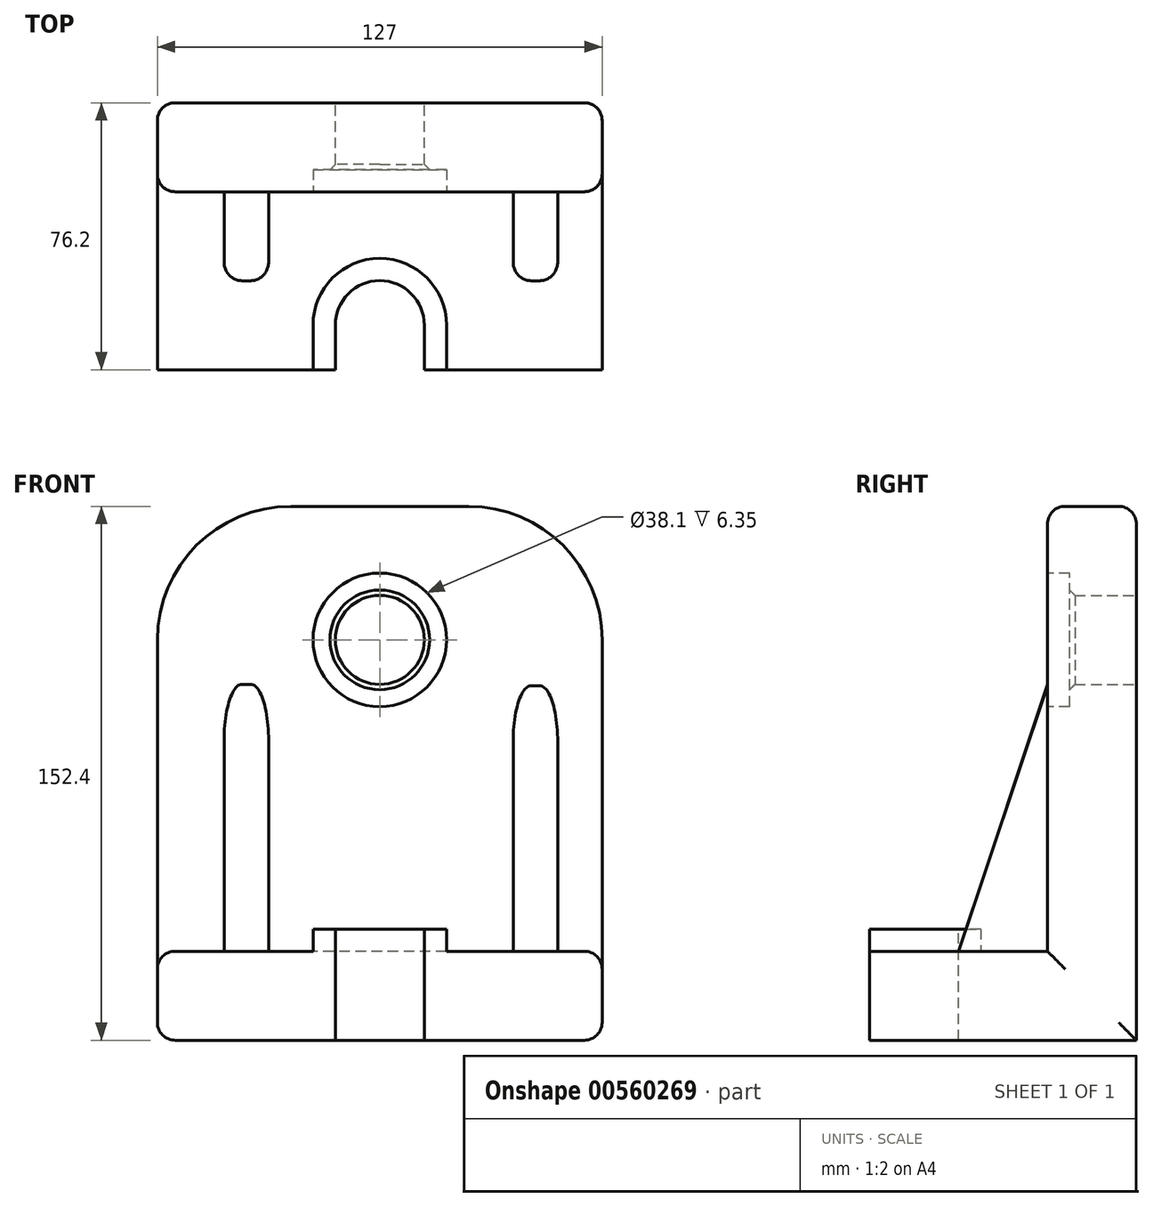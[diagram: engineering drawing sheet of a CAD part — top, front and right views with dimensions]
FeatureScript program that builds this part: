
annotation { "Feature Type Name" : "Feature", "Feature Type Description" : "" }
export const myFeature = defineFeature(function(context is Context, id is Id, definition is map)
    precondition{}
    {
        {
            var Q0;
            Q0=qCreatedBy(makeId("Right.planeOp"),FACE);
            var sketch = newSketch(context, id + "F0", { "sketchPlane" : qUnion([Q0])});
            skLineSegment(sketch, "E0", {"start": v(0, 25.4) * mm, "end": v(0, 152.4) * mm});
            skLineSegment(sketch, "E1", {"start": v(0, 152.4) * mm, "end": v(-25.4, 152.4) * mm});
            skLineSegment(sketch, "E2", {"start": v(-25.4, 152.4) * mm, "end": v(-25.4, 25.4) * mm});
            skLineSegment(sketch, "E3", {"start": v(-25.4, 25.4) * mm, "end": v(-76.2, 25.4) * mm});
            skLineSegment(sketch, "E4", {"start": v(-76.2, 25.4) * mm, "end": v(-76.2, 0) * mm});
            skLineSegment(sketch, "E5", {"start": v(-76.2, 0) * mm, "end": v(0, 0) * mm});
            skLineSegment(sketch, "E6", {"start": v(0, 0) * mm, "end": v(0, 25.4) * mm});
            skSolve(sketch);
        }
        {
            var Q0;
            Q0=makeQuery(id+"F0.imprint","IMPRINT",FACE,{"disambiguationData":[TD([[makeQuery(id+"F0.imprint","IMPRINT",EDGE,{"derivedFrom":sQuery(id+"F0.wireOp",EDGE,"E0")}),1.0]])]});
            extrude(context, id + "F1", {"entities" : qUnion([Q0]), "endBound" : BoundingType.SYMMETRIC, "depth" : 127 * mm, "offsetDistance" : 25.4 * mm});
        }
        {
            var Q0;
            Q0=makeQuery(id+"F1.opExtrude","SWEPT_FACE",FACE,{"disambiguationData":[OSD([sQuery(id+"F0.wireOp",EDGE,"E0"),sQuery(id+"F0.wireOp",EDGE,"E6")])]});
            var sketch = newSketch(context, id + "F2", { "sketchPlane" : qUnion([Q0])});
            skCircle(sketch, "E7", {"center": v(0, 114.3) * mm, "radius": 12.7 * mm});
            skSolve(sketch);
        }
        {
            var Q0;
            Q0=makeQuery(id+"F2.imprint","IMPRINT",FACE,{"disambiguationData":[TD([[makeQuery(id+"F2.imprint","IMPRINT",EDGE,{"derivedFrom":sQuery(id+"F2.wireOp",EDGE,"E7")}),1.0]])]});
            extrude(context, id + "F3", {"entities" : qUnion([Q0]), "operationType" : NewBodyOperationType.REMOVE, "endBound" : BoundingType.THROUGH_ALL, "oppositeDirection" : true, "depth" : 25.4 * mm, "offsetDistance" : 25.4 * mm});
        }
        {
            var Q0;
            Q0=makeQuery(id+"F1.opExtrude","SWEPT_FACE",FACE,{"disambiguationData":[OSD([sQuery(id+"F0.wireOp",EDGE,"E3")])]});
            var sketch = newSketch(context, id + "F4", { "sketchPlane" : qUnion([Q0])});
            skCircle(sketch, "E8", {"center": v(0, -63.5) * mm, "radius": 12.71 * mm});
            skLineSegment(sketch, "E9", {"start": v(-12.71, -63.5) * mm, "end": v(-12.71, -76.2) * mm});
            skLineSegment(sketch, "E10", {"start": v(12.71, -63.5) * mm, "end": v(12.71, -76.2) * mm});
            skSolve(sketch);
        }
        {
            var Q0;
            {var subQ0=sQuery(id+"F4.wireOp",EDGE,"E9");Q0=makeQuery(id+"F4.imprint","IMPRINT",FACE,{"disambiguationData":[TD([[makeQuery(id+"F4.imprint","IMPRINT",EDGE,{"derivedFrom":subQ0}),1.0]])]});}
            var Q1;
            {var subQ0=sQuery(id+"F4.wireOp",EDGE,"E8");var subQ1=makeQuery(id+"F4.imprint","INTERSECT",VERTEX,{"derivedFrom":[subQ0,sQuery(id+"F4.wireOp",EDGE,"E9")]});Q1=makeQuery(id+"F4.imprint","IMPRINT",FACE,{"disambiguationData":[TD([[makeQuery(id+"F4.imprint","IMPRINT",EDGE,{"disambiguationData":[TD([[subQ1,1.0]])],"derivedFrom":subQ0}),1.0]])]});}
            var Q2;
            {var subQ0=sQuery(id+"F4.wireOp",EDGE,"E10");Q2=makeQuery(id+"F4.imprint","IMPRINT",FACE,{"disambiguationData":[TD([[makeQuery(id+"F4.imprint","IMPRINT",EDGE,{"derivedFrom":subQ0}),-1.0]])]});}
            extrude(context, id + "F5", {"entities" : qUnion([Q0, Q1, Q2]), "operationType" : NewBodyOperationType.REMOVE, "endBound" : BoundingType.THROUGH_ALL, "oppositeDirection" : true, "depth" : 25.4 * mm, "offsetDistance" : 25.4 * mm});
        }
        {
            var Q0;
            Q0=qCreatedBy(makeId("Right.planeOp"),FACE);
            cPlane(context, id + "F6", {"entities" : qUnion([Q0]), "cplaneType" : CPlaneType.OFFSET, "offset" : 44.45 * mm, "width" : 152.4 * mm, "height" : 152.4 * mm});
        }
        {
            var Q0;
            Q0=qCreatedBy(id+"F6.planeOp",FACE);
            var sketch = newSketch(context, id + "F7", { "sketchPlane" : qUnion([Q0])});
            skLineSegment(sketch, "E11.0", {"start": v(-25.4, 25.4) * mm, "end": v(-76.2, 25.4) * mm});
            skLineSegment(sketch, "E11.1", {"start": v(-25.4, 151.98) * mm, "end": v(-25.4, 25.4) * mm});
            skLineSegment(sketch, "E12", {"start": v(-76.2, 25.4) * mm, "end": v(-50.8, 25.4) * mm});
            skLineSegment(sketch, "E13", {"start": v(-25.4, 151.98) * mm, "end": v(-25.4, 101.18) * mm});
            skLineSegment(sketch, "E14", {"start": v(-50.8, 25.4) * mm, "end": v(-25.4, 101.18) * mm});
            skSolve(sketch);
        }
        {
            var Q0;
            Q0 = qSketchRegion(id + "F7", true);
            extrude(context, id + "F8", {"entities" : qUnion([Q0]), "operationType" : NewBodyOperationType.ADD, "endBound" : BoundingType.SYMMETRIC, "depth" : 12.7 * mm, "offsetDistance" : 25.4 * mm});
        }
        {
            var Q0;
            Q0=qCreatedBy(makeId("Right.planeOp"),FACE);
            cPlane(context, id + "F9", {"entities" : qUnion([Q0]), "cplaneType" : CPlaneType.OFFSET, "offset" : 44.45 * mm, "oppositeDirection" : true, "width" : 152.4 * mm, "height" : 152.4 * mm});
        }
        {
            var Q0;
            Q0=qCreatedBy(id+"F9.planeOp",FACE);
            var sketch = newSketch(context, id + "F10", { "sketchPlane" : qUnion([Q0])});
            skLineSegment(sketch, "E15.0", {"start": v(-25.4, 101.6) * mm, "end": v(-25.4, 25.4) * mm});
            skLineSegment(sketch, "E15.1", {"start": v(-25.4, 25.4) * mm, "end": v(-50.8, 25.4) * mm});
            skLineSegment(sketch, "E16", {"start": v(-25.4, 101.6) * mm, "end": v(-50.8, 25.4) * mm});
            skSolve(sketch);
        }
        {
            var Q0;
            Q0 = qSketchRegion(id + "F10", true);
            extrude(context, id + "F11", {"entities" : qUnion([Q0]), "operationType" : NewBodyOperationType.ADD, "depth" : 12.7 * mm, "offsetDistance" : 25.4 * mm});
        }
        {
            var Q0;
            Q0=makeQuery(id+"F1.opExtrude","CAP_EDGE",EDGE,{"disambiguationData":[OSD([sQuery(id+"F0.wireOp",EDGE,"E1")])],"isStart":true});
            var Q1;
            Q1=makeQuery(id+"F1.opExtrude","CAP_EDGE",EDGE,{"disambiguationData":[OSD([sQuery(id+"F0.wireOp",EDGE,"E1")])],"isStart":false});
            fillet(context, id + "F12", {"entities" : qUnion([Q0, Q1]), "radius" : 38.1 * mm, "tangentPropagation" : true, "allowEdgeOverflow" : false});
        }
        {
            var Q0;
            Q0=makeQuery(id+"F1.opExtrude","SWEPT_FACE",FACE,{"disambiguationData":[OSD([sQuery(id+"F0.wireOp",EDGE,"E3")])]});
            var sketch = newSketch(context, id + "F13", { "sketchPlane" : qUnion([Q0])});
            skLineSegment(sketch, "E17.0", {"start": v(-19.06, -63.5) * mm, "end": v(-19.06, -76.2) * mm});
            skArc(sketch, "E17.1", {"start": v(19.06, -63.5) * mm, "mid": v(0, -44.44) * mm, "end": v(-19.06, -63.5) * mm});
            skLineSegment(sketch, "E17.2", {"start": v(19.06, -63.5) * mm, "end": v(19.06, -76.2) * mm});
            skSolve(sketch);
        }
        {
            var Q0;
            {var subQ1=sQuery(id+"F13.wireOp",EDGE,"E17.0");Q0=makeQuery(id+"F13.imprint","IMPRINT",FACE,{"disambiguationData":[TD([[makeQuery(id+"F13.imprint","IMPRINT",EDGE,{"derivedFrom":subQ1}),1.0]])]});}
            extrude(context, id + "F14", {"entities" : qUnion([Q0]), "operationType" : NewBodyOperationType.ADD, "depth" : 6.35 * mm, "offsetDistance" : 25.4 * mm});
        }
        {
            var Q0;
            Q0=makeQuery(id+"F1.opExtrude","SWEPT_FACE",FACE,{"disambiguationData":[OSD([sQuery(id+"F0.wireOp",EDGE,"E2")])]});
            var sketch = newSketch(context, id + "F15", { "sketchPlane" : qUnion([Q0])});
            skCircle(sketch, "E18", {"center": v(0, 114.3) * mm, "radius": 19.05 * mm});
            skSolve(sketch);
        }
        {
            var Q0;
            Q0 = qSketchRegion(id + "F15", true);
            extrude(context, id + "F16", {"entities" : qUnion([Q0]), "operationType" : NewBodyOperationType.REMOVE, "oppositeDirection" : true, "depth" : 6.35 * mm, "offsetDistance" : 25.4 * mm});
        }
        {
            var Q0;
            Q0=makeQuery(id+"F16.boolean.opBoolean","COPY",EDGE,{"derivedFrom":makeQuery(id+"F16.opExtrude","CAP_EDGE",EDGE,{"disambiguationData":[OSD([sQuery(id+"F15.wireOp",EDGE,"E18")])],"isStart":true})});
            var Q1;
            Q1=makeQuery(id+"F16.boolean.opBoolean","INTERSECT",EDGE,{"derivedFrom":[makeQuery(id+"F3.boolean.opBoolean","COPY",FACE,{"derivedFrom":makeQuery(id+"F3.opExtrude","SWEPT_FACE",FACE,{"disambiguationData":[OSD([sQuery(id+"F2.wireOp",EDGE,"E7")])]})}),makeQuery(id+"F16.opExtrude","CAP_FACE",FACE,{"disambiguationData":[OSD([sQuery(id+"F15.wireOp",EDGE,"E18")])],"isStart":false})]});
            chamfer(context, id + "F17", {"entities" : qUnion([Q0, Q1]), "width" : 1.52 * mm, "tangentPropagation" : true});
        }
        {
            var Q0;
            Q0=makeQuery(id+"F12.opFillet","BLEND_EDGE",EDGE,{"blendedFrom":[makeQuery(id+"F1.opExtrude","CAP_EDGE",EDGE,{"disambiguationData":[OSD([sQuery(id+"F0.wireOp",EDGE,"E1")])],"isStart":false}),makeQuery(id+"F1.opExtrude","SWEPT_FACE",FACE,{"disambiguationData":[OSD([sQuery(id+"F0.wireOp",EDGE,"E2")])]})],"blendedInto":[makeQuery(id+"F1.opExtrude","SWEPT_FACE",FACE,{"disambiguationData":[OSD([sQuery(id+"F0.wireOp",EDGE,"E2")])]})]});
            var Q1;
            Q1=makeQuery(id+"F1.opExtrude","SWEPT_EDGE",EDGE,{"disambiguationData":[OSD([sQuery(id+"F0.wireOp",EDGE,"E1"),sQuery(id+"F0.wireOp",EDGE,"E2")])]});
            var Q2;
            Q2=makeQuery(id+"F12.opFillet","BLEND_EDGE",EDGE,{"blendedFrom":[makeQuery(id+"F1.opExtrude","CAP_EDGE",EDGE,{"disambiguationData":[OSD([sQuery(id+"F0.wireOp",EDGE,"E1")])],"isStart":true}),makeQuery(id+"F1.opExtrude","SWEPT_FACE",FACE,{"disambiguationData":[OSD([sQuery(id+"F0.wireOp",EDGE,"E2")])]})],"blendedInto":[makeQuery(id+"F1.opExtrude","SWEPT_FACE",FACE,{"disambiguationData":[OSD([sQuery(id+"F0.wireOp",EDGE,"E2")])]})]});
            var Q3;
            Q3=makeQuery(id+"F1.opExtrude","CAP_EDGE",EDGE,{"disambiguationData":[OSD([sQuery(id+"F0.wireOp",EDGE,"E2")])],"isStart":true});
            var Q4;
            Q4=makeQuery(id+"F1.opExtrude","CAP_EDGE",EDGE,{"disambiguationData":[OSD([sQuery(id+"F0.wireOp",EDGE,"E2")])],"isStart":false});
            var Q5;
            Q5=makeQuery(id+"F8.opExtrude","CAP_EDGE",EDGE,{"disambiguationData":[OSD([sQuery(id+"F7.wireOp",EDGE,"E11.1")])],"isStart":false});
            var Q6;
            Q6=makeQuery(id+"F11.opExtrude","CAP_EDGE",EDGE,{"disambiguationData":[OSD([sQuery(id+"F10.wireOp",EDGE,"E15.0")])],"isStart":false});
            var Q7;
            Q7=makeQuery(id+"F8.opExtrude","CAP_EDGE",EDGE,{"disambiguationData":[OSD([sQuery(id+"F7.wireOp",EDGE,"E11.1")])],"isStart":true});
            var Q8;
            Q8=makeQuery(id+"F11.opExtrude","CAP_EDGE",EDGE,{"disambiguationData":[OSD([sQuery(id+"F10.wireOp",EDGE,"E15.0")])],"isStart":true});
            var Q9;
            Q9=makeQuery(id+"F11.opExtrude","CAP_EDGE",EDGE,{"disambiguationData":[OSD([sQuery(id+"F10.wireOp",EDGE,"E16")])],"isStart":true});
            var Q10;
            Q10=makeQuery(id+"F11.opExtrude","CAP_EDGE",EDGE,{"disambiguationData":[OSD([sQuery(id+"F10.wireOp",EDGE,"E16")])],"isStart":false});
            var Q11;
            Q11=makeQuery(id+"F8.opExtrude","CAP_EDGE",EDGE,{"disambiguationData":[OSD([sQuery(id+"F7.wireOp",EDGE,"E14")])],"isStart":true});
            var Q12;
            Q12=makeQuery(id+"F8.opExtrude","CAP_EDGE",EDGE,{"disambiguationData":[OSD([sQuery(id+"F7.wireOp",EDGE,"E14")])],"isStart":false});
            var Q13;
            Q13=makeQuery(id+"F14.opExtrude","CAP_EDGE",EDGE,{"disambiguationData":[OSD([sQuery(id+"F13.wireOp",EDGE,"E17.2")])],"isStart":true});
            var Q14;
            Q14=makeQuery(id+"F14.opExtrude","CAP_EDGE",EDGE,{"disambiguationData":[OSD([sQuery(id+"F13.wireOp",EDGE,"E17.1")])],"isStart":true});
            var Q15;
            Q15=makeQuery(id+"F14.opExtrude","CAP_EDGE",EDGE,{"disambiguationData":[OSD([sQuery(id+"F13.wireOp",EDGE,"E17.0")])],"isStart":true});
            var Q16;
            Q16=makeQuery(id+"F1.opExtrude","CAP_EDGE",EDGE,{"disambiguationData":[OSD([sQuery(id+"F0.wireOp",EDGE,"E3")])],"isStart":true});
            var Q17;
            Q17=makeQuery(id+"F1.opExtrude","CAP_EDGE",EDGE,{"disambiguationData":[OSD([sQuery(id+"F0.wireOp",EDGE,"E5")])],"isStart":true});
            var Q18;
            Q18=makeQuery(id+"F1.opExtrude","CAP_EDGE",EDGE,{"disambiguationData":[OSD([sQuery(id+"F0.wireOp",EDGE,"E0"),sQuery(id+"F0.wireOp",EDGE,"E6")])],"isStart":true});
            var Q19;
            Q19=makeQuery(id+"F12.opFillet","BLEND_EDGE",EDGE,{"blendedFrom":[makeQuery(id+"F1.opExtrude","CAP_EDGE",EDGE,{"disambiguationData":[OSD([sQuery(id+"F0.wireOp",EDGE,"E1")])],"isStart":true}),makeQuery(id+"F1.opExtrude","SWEPT_FACE",FACE,{"disambiguationData":[OSD([sQuery(id+"F0.wireOp",EDGE,"E0"),sQuery(id+"F0.wireOp",EDGE,"E6")])]})],"blendedInto":[makeQuery(id+"F1.opExtrude","SWEPT_FACE",FACE,{"disambiguationData":[OSD([sQuery(id+"F0.wireOp",EDGE,"E0"),sQuery(id+"F0.wireOp",EDGE,"E6")])]})]});
            var Q20;
            Q20=makeQuery(id+"F1.opExtrude","SWEPT_EDGE",EDGE,{"disambiguationData":[OSD([sQuery(id+"F0.wireOp",EDGE,"E0"),sQuery(id+"F0.wireOp",EDGE,"E1")])]});
            var Q21;
            Q21=makeQuery(id+"F12.opFillet","BLEND_EDGE",EDGE,{"blendedFrom":[makeQuery(id+"F1.opExtrude","CAP_EDGE",EDGE,{"disambiguationData":[OSD([sQuery(id+"F0.wireOp",EDGE,"E1")])],"isStart":false}),makeQuery(id+"F1.opExtrude","SWEPT_FACE",FACE,{"disambiguationData":[OSD([sQuery(id+"F0.wireOp",EDGE,"E0"),sQuery(id+"F0.wireOp",EDGE,"E6")])]})],"blendedInto":[makeQuery(id+"F1.opExtrude","SWEPT_FACE",FACE,{"disambiguationData":[OSD([sQuery(id+"F0.wireOp",EDGE,"E0"),sQuery(id+"F0.wireOp",EDGE,"E6")])]})]});
            var Q22;
            Q22=makeQuery(id+"F1.opExtrude","CAP_EDGE",EDGE,{"disambiguationData":[OSD([sQuery(id+"F0.wireOp",EDGE,"E0"),sQuery(id+"F0.wireOp",EDGE,"E6")])],"isStart":false});
            var Q23;
            Q23=makeQuery(id+"F1.opExtrude","CAP_EDGE",EDGE,{"disambiguationData":[OSD([sQuery(id+"F0.wireOp",EDGE,"E5")])],"isStart":false});
            var Q24;
            Q24=makeQuery(id+"F8.opExtrude","CAP_EDGE",EDGE,{"disambiguationData":[OSD([sQuery(id+"F7.wireOp",EDGE,"E11.0")])],"isStart":false});
            var Q25;
            Q25=makeQuery(id+"F8.opExtrude","CAP_EDGE",EDGE,{"disambiguationData":[OSD([sQuery(id+"F7.wireOp",EDGE,"E11.0")])],"isStart":true});
            var Q26;
            Q26=makeQuery(id+"F11.opExtrude","CAP_EDGE",EDGE,{"disambiguationData":[OSD([sQuery(id+"F10.wireOp",EDGE,"E15.1")])],"isStart":true});
            var Q27;
            Q27=makeQuery(id+"F11.opExtrude","CAP_EDGE",EDGE,{"disambiguationData":[OSD([sQuery(id+"F10.wireOp",EDGE,"E15.1")])],"isStart":false});
            var Q28;
            Q28=makeQuery(id+"F1.opExtrude","CAP_EDGE",EDGE,{"disambiguationData":[OSD([sQuery(id+"F0.wireOp",EDGE,"E3")])],"isStart":false});
            fillet(context, id + "F18", {"entities" : qUnion([Q0, Q1, Q2, Q3, Q4, Q5, Q6, Q7, Q8, Q9, Q10, Q11, Q12, Q13, Q14, Q15, Q16, Q17, Q18, Q19, Q20, Q21, Q22, Q23, Q24, Q25, Q26, Q27, Q28]), "radius" : 5.08 * mm, "tangentPropagation" : true, "allowEdgeOverflow" : false});
        }
    });
